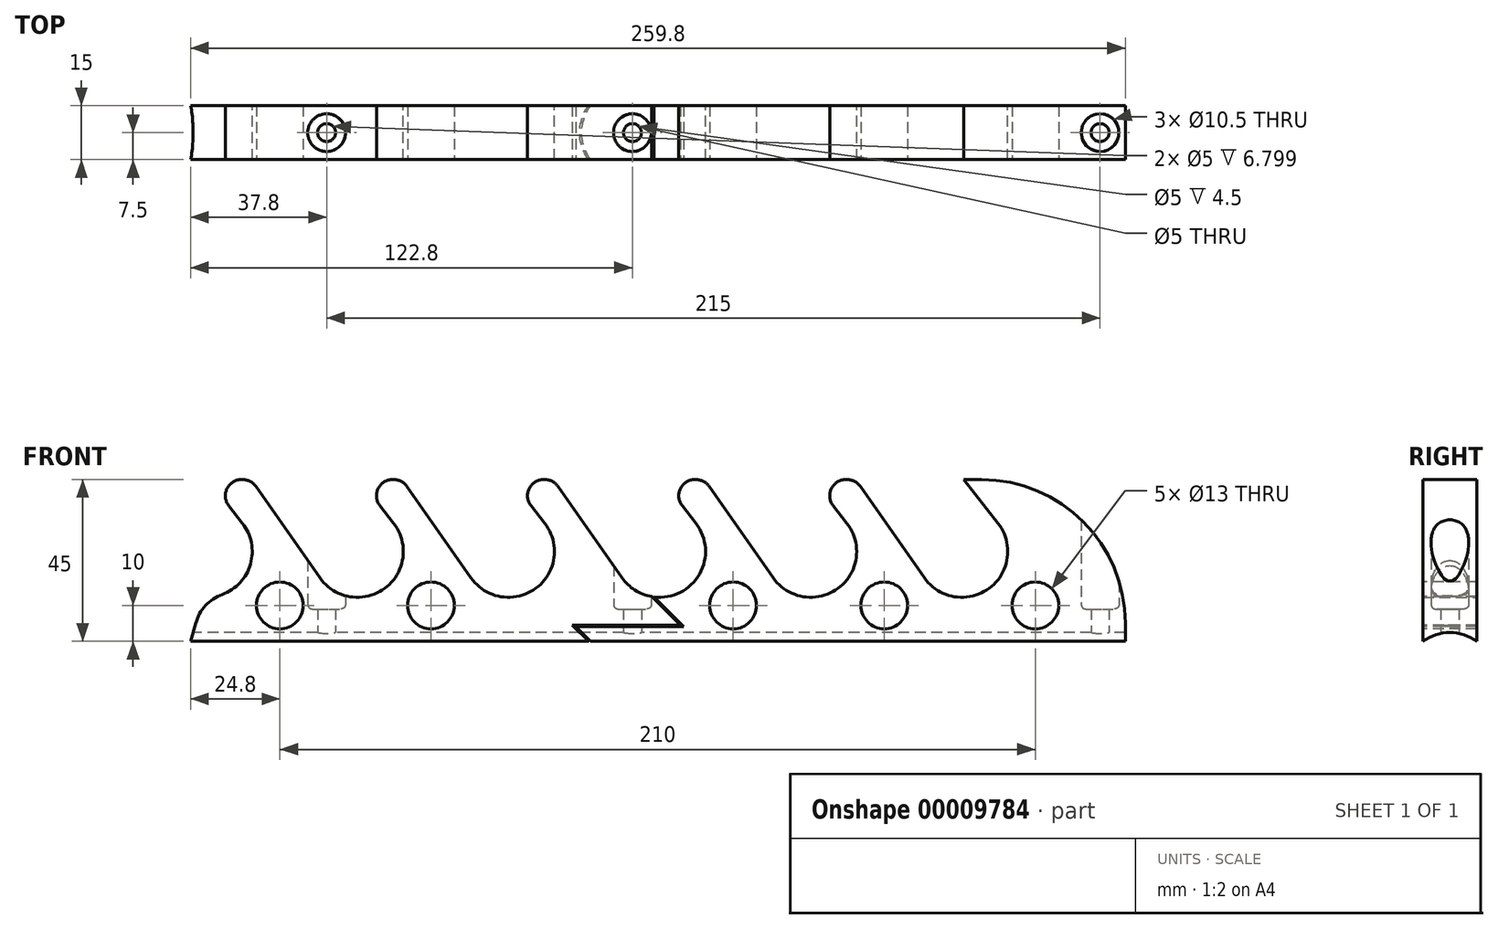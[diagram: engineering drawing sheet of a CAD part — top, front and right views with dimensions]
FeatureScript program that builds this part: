
annotation { "Feature Type Name" : "Feature", "Feature Type Description" : "" }
export const myFeature = defineFeature(function(context is Context, id is Id, definition is map)
    precondition{}
    {
        {
            var Q0;
            Q0=qCreatedBy(makeId("Front.planeOp"),FACE);
            var sketch = newSketch(context, id + "F0", { "sketchPlane" : qUnion([Q0])});
            skLineSegment(sketch, "E0.bottom", {"start": v(0, 0) * mm, "end": v(262, 0) * mm});
            skLineSegment(sketch, "E0.top", {"start": v(0, 45) * mm, "end": v(262, 45) * mm});
            skLineSegment(sketch, "E0.left", {"start": v(0, 0) * mm, "end": v(0, 45) * mm});
            skLineSegment(sketch, "E0.right", {"start": v(262, 0) * mm, "end": v(262, 45) * mm});
            skSolve(sketch);
        }
        {
            var Q0;
            Q0=makeQuery(id+"F0.imprint","IMPRINT",FACE,{"disambiguationData":[TD([[makeQuery(id+"F0.imprint","IMPRINT",EDGE,{"derivedFrom":sQuery(id+"F0.wireOp",EDGE,"E0.bottom")}),1.0]])]});
            extrude(context, id + "F1", {"entities" : qUnion([Q0]), "depth" : 15 * mm / 2});
        }
        {
            var Q0;
            Q0=qCreatedBy(makeId("Front.planeOp"),FACE);
            var sketch = newSketch(context, id + "F2", { "sketchPlane" : qUnion([Q0])});
            skArc(sketch, "E1", {"start": v(38.12, 17.69) * mm, "mid": v(56.15, 14.75) * mm, "end": v(58.62, 32.85) * mm});
            skLineSegment(sketch, "E2", {"start": v(38.12, 17.69) * mm, "end": v(19, 45) * mm});
            skLineSegment(sketch, "E3", {"start": v(19, 45) * mm, "end": v(49.12, 45) * mm});
            skLineSegment(sketch, "E4", {"start": v(49.12, 45) * mm, "end": v(58.62, 32.85) * mm});
            skLineSegment(sketch, "E5.1.0.0", {"start": v(91.12, 45) * mm, "end": v(100.62, 32.85) * mm});
            skLineSegment(sketch, "E5.1.0.1", {"start": v(61, 45) * mm, "end": v(91.12, 45) * mm});
            skLineSegment(sketch, "E5.1.0.2", {"start": v(80.12, 17.69) * mm, "end": v(61, 45) * mm});
            skArc(sketch, "E5.1.0.3", {"start": v(80.12, 17.69) * mm, "mid": v(98.15, 14.75) * mm, "end": v(100.62, 32.85) * mm});
            skLineSegment(sketch, "E5.2.0.0", {"start": v(133.12, 45) * mm, "end": v(142.62, 32.85) * mm});
            skLineSegment(sketch, "E5.2.0.1", {"start": v(103, 45) * mm, "end": v(133.12, 45) * mm});
            skLineSegment(sketch, "E5.2.0.2", {"start": v(122.12, 17.69) * mm, "end": v(103, 45) * mm});
            skArc(sketch, "E5.2.0.3", {"start": v(122.12, 17.69) * mm, "mid": v(140.15, 14.75) * mm, "end": v(142.62, 32.85) * mm});
            skLineSegment(sketch, "E5.3.0.0", {"start": v(175.12, 45) * mm, "end": v(184.62, 32.85) * mm});
            skLineSegment(sketch, "E5.3.0.1", {"start": v(145, 45) * mm, "end": v(175.12, 45) * mm});
            skLineSegment(sketch, "E5.3.0.2", {"start": v(164.12, 17.69) * mm, "end": v(145, 45) * mm});
            skArc(sketch, "E5.3.0.3", {"start": v(164.12, 17.69) * mm, "mid": v(182.15, 14.75) * mm, "end": v(184.62, 32.85) * mm});
            skLineSegment(sketch, "E5.4.0.0", {"start": v(217.12, 45) * mm, "end": v(226.62, 32.85) * mm});
            skLineSegment(sketch, "E5.4.0.1", {"start": v(187, 45) * mm, "end": v(217.12, 45) * mm});
            skLineSegment(sketch, "E5.4.0.2", {"start": v(206.12, 17.69) * mm, "end": v(187, 45) * mm});
            skArc(sketch, "E5.4.0.3", {"start": v(206.12, 17.69) * mm, "mid": v(224.15, 14.75) * mm, "end": v(226.62, 32.85) * mm});
            skLineSegment(sketch, "E5.direction1", {"start": v(58.62, 32.85) * mm, "end": v(100.62, 32.85) * mm, "construction": true});
            skArc(sketch, "E6.1.0.0", {"start": v(-3.88, 17.69) * mm, "mid": v(14.15, 14.75) * mm, "end": v(16.62, 32.85) * mm});
            skLineSegment(sketch, "E6.1.0.1", {"start": v(-3.88, 17.69) * mm, "end": v(-23, 45) * mm});
            skLineSegment(sketch, "E6.1.0.2", {"start": v(-23, 45) * mm, "end": v(7.12, 45) * mm});
            skLineSegment(sketch, "E6.1.0.3", {"start": v(7.12, 45) * mm, "end": v(16.62, 32.85) * mm});
            skLineSegment(sketch, "E6.direction1", {"start": v(38.12, 17.69) * mm, "end": v(-3.88, 17.69) * mm, "construction": true});
            skSolve(sketch);
        }
        {
            var Q0;
            Q0 = qSketchRegion(id + "F2", true);
            extrude(context, id + "F3", {"entities" : qUnion([Q0]), "operationType" : NewBodyOperationType.REMOVE, "depth" : 25 * mm});
        }
        {
            var Q0;
            Q0=makeQuery(id+"F3.boolean.opBoolean","COPY",EDGE,{"derivedFrom":makeQuery(id+"F3.opExtrude","SWEPT_EDGE",EDGE,{"disambiguationData":[OSD([sQuery(id+"F2.wireOp",EDGE,"E2"),sQuery(id+"F2.wireOp",EDGE,"E3")])]})});
            var Q1;
            Q1=makeQuery(id+"F3.boolean.opBoolean","COPY",EDGE,{"derivedFrom":makeQuery(id+"F3.opExtrude","SWEPT_EDGE",EDGE,{"disambiguationData":[OSD([sQuery(id+"F2.wireOp",EDGE,"E3"),sQuery(id+"F2.wireOp",EDGE,"E4")])]})});
            var Q2;
            Q2=makeQuery(id+"F3.boolean.opBoolean","COPY",EDGE,{"derivedFrom":makeQuery(id+"F3.opExtrude","SWEPT_EDGE",EDGE,{"disambiguationData":[OSD([sQuery(id+"F2.wireOp",EDGE,"E5.1.0.1"),sQuery(id+"F2.wireOp",EDGE,"E5.1.0.2")])]})});
            var Q3;
            Q3=makeQuery(id+"F3.boolean.opBoolean","COPY",EDGE,{"derivedFrom":makeQuery(id+"F3.opExtrude","SWEPT_EDGE",EDGE,{"disambiguationData":[OSD([sQuery(id+"F2.wireOp",EDGE,"E5.1.0.0"),sQuery(id+"F2.wireOp",EDGE,"E5.1.0.1")])]})});
            var Q4;
            Q4=makeQuery(id+"F3.boolean.opBoolean","COPY",EDGE,{"derivedFrom":makeQuery(id+"F3.opExtrude","SWEPT_EDGE",EDGE,{"disambiguationData":[OSD([sQuery(id+"F2.wireOp",EDGE,"E5.2.0.1"),sQuery(id+"F2.wireOp",EDGE,"E5.2.0.2")])]})});
            var Q5;
            Q5=makeQuery(id+"F3.boolean.opBoolean","COPY",EDGE,{"derivedFrom":makeQuery(id+"F3.opExtrude","SWEPT_EDGE",EDGE,{"disambiguationData":[OSD([sQuery(id+"F2.wireOp",EDGE,"E5.2.0.0"),sQuery(id+"F2.wireOp",EDGE,"E5.2.0.1")])]})});
            var Q6;
            Q6=makeQuery(id+"F3.boolean.opBoolean","COPY",EDGE,{"derivedFrom":makeQuery(id+"F3.opExtrude","SWEPT_EDGE",EDGE,{"disambiguationData":[OSD([sQuery(id+"F2.wireOp",EDGE,"E5.3.0.1"),sQuery(id+"F2.wireOp",EDGE,"E5.3.0.2")])]})});
            var Q7;
            Q7=makeQuery(id+"F3.boolean.opBoolean","COPY",EDGE,{"derivedFrom":makeQuery(id+"F3.opExtrude","SWEPT_EDGE",EDGE,{"disambiguationData":[OSD([sQuery(id+"F2.wireOp",EDGE,"E5.3.0.0"),sQuery(id+"F2.wireOp",EDGE,"E5.3.0.1")])]})});
            var Q8;
            Q8=makeQuery(id+"F3.boolean.opBoolean","COPY",EDGE,{"derivedFrom":makeQuery(id+"F3.opExtrude","SWEPT_EDGE",EDGE,{"disambiguationData":[OSD([sQuery(id+"F2.wireOp",EDGE,"E5.4.0.1"),sQuery(id+"F2.wireOp",EDGE,"E5.4.0.2")])]})});
            var Q9;
            Q9=makeQuery(id+"F3.boolean.opBoolean","COPY",EDGE,{"derivedFrom":makeQuery(id+"F3.opExtrude","SWEPT_EDGE",EDGE,{"disambiguationData":[OSD([sQuery(id+"F2.wireOp",EDGE,"E5.4.0.0"),sQuery(id+"F2.wireOp",EDGE,"E5.4.0.1")])]})});
            var Q10;
            Q10=makeQuery(id+"F3.boolean.opBoolean","COPY",EDGE,{"derivedFrom":makeQuery(id+"F3.opExtrude","SWEPT_EDGE",EDGE,{"disambiguationData":[OSD([sQuery(id+"F2.wireOp",EDGE,"E6.1.0.2"),sQuery(id+"F2.wireOp",EDGE,"E6.1.0.3")])]})});
            fillet(context, id + "F4", {"entities" : qUnion([Q0, Q1, Q2, Q3, Q4, Q5, Q6, Q7, Q8, Q9, Q10]), "radius" : 4.5 * mm, "tangentPropagation" : true, "allowEdgeOverflow" : false});
        }
        {
            var Q0;
            Q0=makeQuery(id+"F3.boolean.opBoolean","INTERSECT",EDGE,{"derivedFrom":[makeQuery(id+"F1.opExtrude","SWEPT_FACE",FACE,{"disambiguationData":[OSD([sQuery(id+"F0.wireOp",EDGE,"E0.left")])]}),makeQuery(id+"F3.opExtrude","SWEPT_FACE",FACE,{"disambiguationData":[OSD([sQuery(id+"F2.wireOp",EDGE,"E6.1.0.0")])]})]});
            chamfer(context, id + "F5", {"entities" : qUnion([Q0]), "chamferType" : ChamferType.OFFSET_ANGLE, "width" : 26.1 * mm, "oppositeDirection" : false, "angle" : 40 * degree, "tangentPropagation" : true});
        }
        {
            var Q0;
            Q0=makeQuery(id+"F3.boolean.opBoolean","INTERSECT",EDGE,{"derivedFrom":[makeQuery(id+"F1.opExtrude","SWEPT_FACE",FACE,{"disambiguationData":[OSD([sQuery(id+"F0.wireOp",EDGE,"E0.left")])]}),makeQuery(id+"F3.opExtrude","SWEPT_FACE",FACE,{"disambiguationData":[OSD([sQuery(id+"F2.wireOp",EDGE,"E6.1.0.0")])]})]});
            var Q1;
            {var subQ0=makeQuery(id+"F3.opExtrude","SWEPT_FACE",FACE,{"disambiguationData":[OSD([sQuery(id+"F2.wireOp",EDGE,"E6.1.0.0")])]});Q1=makeQuery(id+"F5.opChamfer","BLEND_EDGE",EDGE,{"blendedFrom":[makeQuery(id+"F3.boolean.opBoolean","INTERSECT",EDGE,{"derivedFrom":[makeQuery(id+"F1.opExtrude","SWEPT_FACE",FACE,{"disambiguationData":[OSD([sQuery(id+"F0.wireOp",EDGE,"E0.left")])]}),subQ0]}),makeQuery(id+"F3.boolean.opBoolean","COPY",FACE,{"derivedFrom":subQ0})],"blendedInto":[makeQuery(id+"F3.boolean.opBoolean","COPY",FACE,{"derivedFrom":subQ0})]});}
            fillet(context, id + "F6", {"entities" : qUnion([Q0, Q1]), "radius" : 12 * mm, "tangentPropagation" : true, "allowEdgeOverflow" : false});
        }
        {
            var Q0;
            Q0=makeQuery(id+"F1.opExtrude","SWEPT_EDGE",EDGE,{"disambiguationData":[OSD([sQuery(id+"F0.wireOp",EDGE,"E0.top"),sQuery(id+"F0.wireOp",EDGE,"E0.right")])]});
            fillet(context, id + "F7", {"entities" : qUnion([Q0]), "radius" : 40 * mm, "tangentPropagation" : true, "allowEdgeOverflow" : false});
        }
        {
            var Q0;
            Q0=makeQuery(id+"F1.opExtrude","SWEPT_BODY",BODY,{"disambiguationData":[OSD([sQuery(id+"F0.wireOp",EDGE,"E0.bottom"),sQuery(id+"F0.wireOp",EDGE,"E0.top"),sQuery(id+"F0.wireOp",EDGE,"E0.left"),sQuery(id+"F0.wireOp",EDGE,"E0.right")])]});
            var Q1;
            Q1=makeQuery(id+"F1.opExtrude","CAP_FACE",FACE,{"disambiguationData":[OSD([sQuery(id+"F0.wireOp",EDGE,"E0.bottom"),sQuery(id+"F0.wireOp",EDGE,"E0.top"),sQuery(id+"F0.wireOp",EDGE,"E0.left"),sQuery(id+"F0.wireOp",EDGE,"E0.right")])],"isStart":true});
            mirror(context, id + "F8", {"operationType" : NewBodyOperationType.ADD, "entities" : qUnion([Q0]), "mirrorPlane" : qUnion([Q1])});
        }
        {
            var Q0;
            Q0=makeQuery(id+"F1.opExtrude","CAP_FACE",FACE,{"disambiguationData":[OSD([sQuery(id+"F0.wireOp",EDGE,"E0.bottom"),sQuery(id+"F0.wireOp",EDGE,"E0.top"),sQuery(id+"F0.wireOp",EDGE,"E0.left"),sQuery(id+"F0.wireOp",EDGE,"E0.right")])],"isStart":false});
            var sketch = newSketch(context, id + "F9", { "sketchPlane" : qUnion([Q0])});
            skCircle(sketch, "E7", {"center": v(27, 10) * mm, "radius": 6.5 * mm});
            skCircle(sketch, "E8.1.0.0", {"center": v(69, 10) * mm, "radius": 6.5 * mm});
            skCircle(sketch, "E8.3.0.0", {"center": v(153, 10) * mm, "radius": 6.5 * mm});
            skCircle(sketch, "E8.4.0.0", {"center": v(195, 10) * mm, "radius": 6.5 * mm});
            skCircle(sketch, "E8.5.0.0", {"center": v(237, 10) * mm, "radius": 6.5 * mm});
            skLineSegment(sketch, "E8.direction1", {"start": v(27, 10) * mm, "end": v(69, 10) * mm, "construction": true});
            skSolve(sketch);
        }
        {
            var Q0;
            Q0 = qSketchRegion(id + "F9", true);
            extrude(context, id + "F10", {"entities" : qUnion([Q0]), "operationType" : NewBodyOperationType.REMOVE, "endBound" : BoundingType.THROUGH_ALL, "oppositeDirection" : true, "depth" : 25 * mm});
        }
        {
            var Q0;
            {var subQ0=makeQuery(id+"F1.opExtrude","SWEPT_FACE",FACE,{"disambiguationData":[OSD([sQuery(id+"F0.wireOp",EDGE,"E0.bottom")])]});Q0=makeQuery(id+"F8.boolean.opBoolean","MERGE",FACE,{"derivedFrom":[subQ0,makeQuery(id+"F8.opPattern","COPY",FACE,{"derivedFrom":subQ0,"instanceName":"1"})]});}
            var sketch = newSketch(context, id + "F11", { "sketchPlane" : qUnion([Q0])});
            skCircle(sketch, "E9", {"center": v(40, 0) * mm, "radius": 2.5 * mm});
            skCircle(sketch, "E10", {"center": v(125, 0) * mm, "radius": 2.5 * mm});
            skCircle(sketch, "E11", {"center": v(255, 0) * mm, "radius": 2.5 * mm});
            skSolve(sketch);
        }
        {
            var Q0;
            Q0 = qSketchRegion(id + "F11", true);
            extrude(context, id + "F12", {"entities" : qUnion([Q0]), "operationType" : NewBodyOperationType.REMOVE, "endBound" : BoundingType.UP_TO_NEXT, "oppositeDirection" : true, "depth" : 25 * mm});
        }
        {
            var Q0;
            Q0=qCreatedBy(makeId("Front.planeOp"),FACE);
            var sketch = newSketch(context, id + "F13", { "sketchPlane" : qUnion([Q0])});
            skLineSegment(sketch, "E12", {"start": v(108.3, 4.5) * mm, "end": v(138.3, 4.5) * mm});
            skLineSegment(sketch, "E13", {"start": v(138.3, 4.5) * mm, "end": v(130.35, 12.44) * mm});
            skLineSegment(sketch, "E14", {"start": v(108.3, 4.5) * mm, "end": v(112.8, 0) * mm});
            skLineSegment(sketch, "E15", {"start": v(131.01, 12.35) * mm, "end": v(139.26, 4.1) * mm});
            skLineSegment(sketch, "E16", {"start": v(139.26, 4.1) * mm, "end": v(109.26, 4.1) * mm});
            skLineSegment(sketch, "E17", {"start": v(109.26, 4.1) * mm, "end": v(113.36, 0) * mm});
            skLineSegment(sketch, "E18", {"start": v(113.36, 0) * mm, "end": v(112.8, 0) * mm});
            skArc(sketch, "E19", {"start": v(130.35, 12.44) * mm, "mid": v(130.68, 12.4) * mm, "end": v(131.01, 12.35) * mm});
            skSolve(sketch);
        }
        {
            var Q0;
            Q0 = qSketchRegion(id + "F13", true);
            extrude(context, id + "F14", {"entities" : qUnion([Q0]), "operationType" : NewBodyOperationType.REMOVE, "endBound" : BoundingType.THROUGH_ALL, "oppositeDirection" : true, "depth" : 25 * mm, "hasSecondDirection" : true, "secondDirectionBound" : SecondDirectionBoundingType.THROUGH_ALL, "secondDirectionOppositeDirection" : false, "secondDirectionDepth" : 25 * mm});
        }
        {
            var Q0;
            {var subQ0=sQuery(id+"F0.wireOp",EDGE,"E0.bottom");var subQ1=makeQuery(id+"F1.opExtrude","SWEPT_FACE",FACE,{"disambiguationData":[OSD([subQ0])]});var subQ2=sQuery(id+"F0.wireOp",EDGE,"E0.left");var subQ4=makeQuery(id+"F1.opExtrude","SWEPT_FACE",FACE,{"disambiguationData":[OSD([subQ2])]});Q0=makeQuery(id+"F14.boolean.opBoolean","SPLIT",FACE,{"disambiguationData":[TD([subQ4])],"derivedFrom":makeQuery(id+"F8.boolean.opBoolean","MERGE",FACE,{"derivedFrom":[subQ1,makeQuery(id+"F8.opPattern","COPY",FACE,{"derivedFrom":subQ1,"instanceName":"1"})]})});}
            var Q1;
            {var subQ0=sQuery(id+"F0.wireOp",EDGE,"E0.bottom");var subQ1=makeQuery(id+"F1.opExtrude","SWEPT_FACE",FACE,{"disambiguationData":[OSD([subQ0])]});Q1=makeQuery(id+"F14.boolean.opBoolean","SPLIT",FACE,{"disambiguationData":[TD([makeQuery(id+"F12.boolean.opBoolean","COPY",FACE,{"derivedFrom":makeQuery(id+"F12.opExtrude","SWEPT_FACE",FACE,{"disambiguationData":[OSD([sQuery(id+"F11.wireOp",EDGE,"E9")])]})})])],"derivedFrom":makeQuery(id+"F8.boolean.opBoolean","MERGE",FACE,{"derivedFrom":[subQ1,makeQuery(id+"F8.opPattern","COPY",FACE,{"derivedFrom":subQ1,"instanceName":"1"})]})});}
            cPlane(context, id + "F15", {"entities" : qUnion([Q0, Q1]), "cplaneType" : CPlaneType.OFFSET, "offset" : 9 * mm, "oppositeDirection" : true, "width" : 150 * mm, "height" : 150 * mm});
        }
        {
            var Q0;
            Q0=qCreatedBy(id+"F15.planeOp",FACE);
            var sketch = newSketch(context, id + "F16", { "sketchPlane" : qUnion([Q0])});
            skCircle(sketch, "E20", {"center": v(40, 0) * mm, "radius": 5.25 * mm});
            skCircle(sketch, "E21", {"center": v(125, 0) * mm, "radius": 5.25 * mm});
            skCircle(sketch, "E22", {"center": v(255, 0) * mm, "radius": 5.25 * mm});
            skSolve(sketch);
        }
        {
            var Q0;
            Q0 = qSketchRegion(id + "F16", true);
            extrude(context, id + "F17", {"entities" : qUnion([Q0]), "operationType" : NewBodyOperationType.REMOVE, "endBound" : BoundingType.THROUGH_ALL, "oppositeDirection" : true, "depth" : 25 * mm});
        }
        {
            var Q0;
            Q0=qCreatedBy(makeId("Right.planeOp"),FACE);
            var sketch = newSketch(context, id + "F18", { "sketchPlane" : qUnion([Q0])});
            skCircle(sketch, "E23", {"center": v(0, -10.25) * mm, "radius": 12.7 * mm});
            skSolve(sketch);
        }
        {
            var Q0;
            Q0 = qSketchRegion(id + "F18", true);
            extrude(context, id + "F19", {"entities" : qUnion([Q0]), "operationType" : NewBodyOperationType.REMOVE, "endBound" : BoundingType.THROUGH_ALL, "depth" : 25 * mm});
        }
        {
            var Q0;
            Q0=makeQuery(id+"F17.boolean.opBoolean","COPY",EDGE,{"derivedFrom":makeQuery(id+"F17.opExtrude","CAP_EDGE",EDGE,{"disambiguationData":[OSD([sQuery(id+"F16.wireOp",EDGE,"E20")])],"isStart":true})});
            var Q1;
            Q1=makeQuery(id+"F17.boolean.opBoolean","COPY",EDGE,{"derivedFrom":makeQuery(id+"F17.opExtrude","CAP_EDGE",EDGE,{"disambiguationData":[OSD([sQuery(id+"F16.wireOp",EDGE,"E21")])],"isStart":true})});
            var Q2;
            Q2=makeQuery(id+"F17.boolean.opBoolean","COPY",EDGE,{"derivedFrom":makeQuery(id+"F17.opExtrude","CAP_EDGE",EDGE,{"disambiguationData":[OSD([sQuery(id+"F16.wireOp",EDGE,"E22")])],"isStart":true})});
            fillet(context, id + "F20", {"entities" : qUnion([Q0, Q1, Q2]), "radius" : 1.3 * mm, "tangentPropagation" : true, "allowEdgeOverflow" : false});
        }
    });
